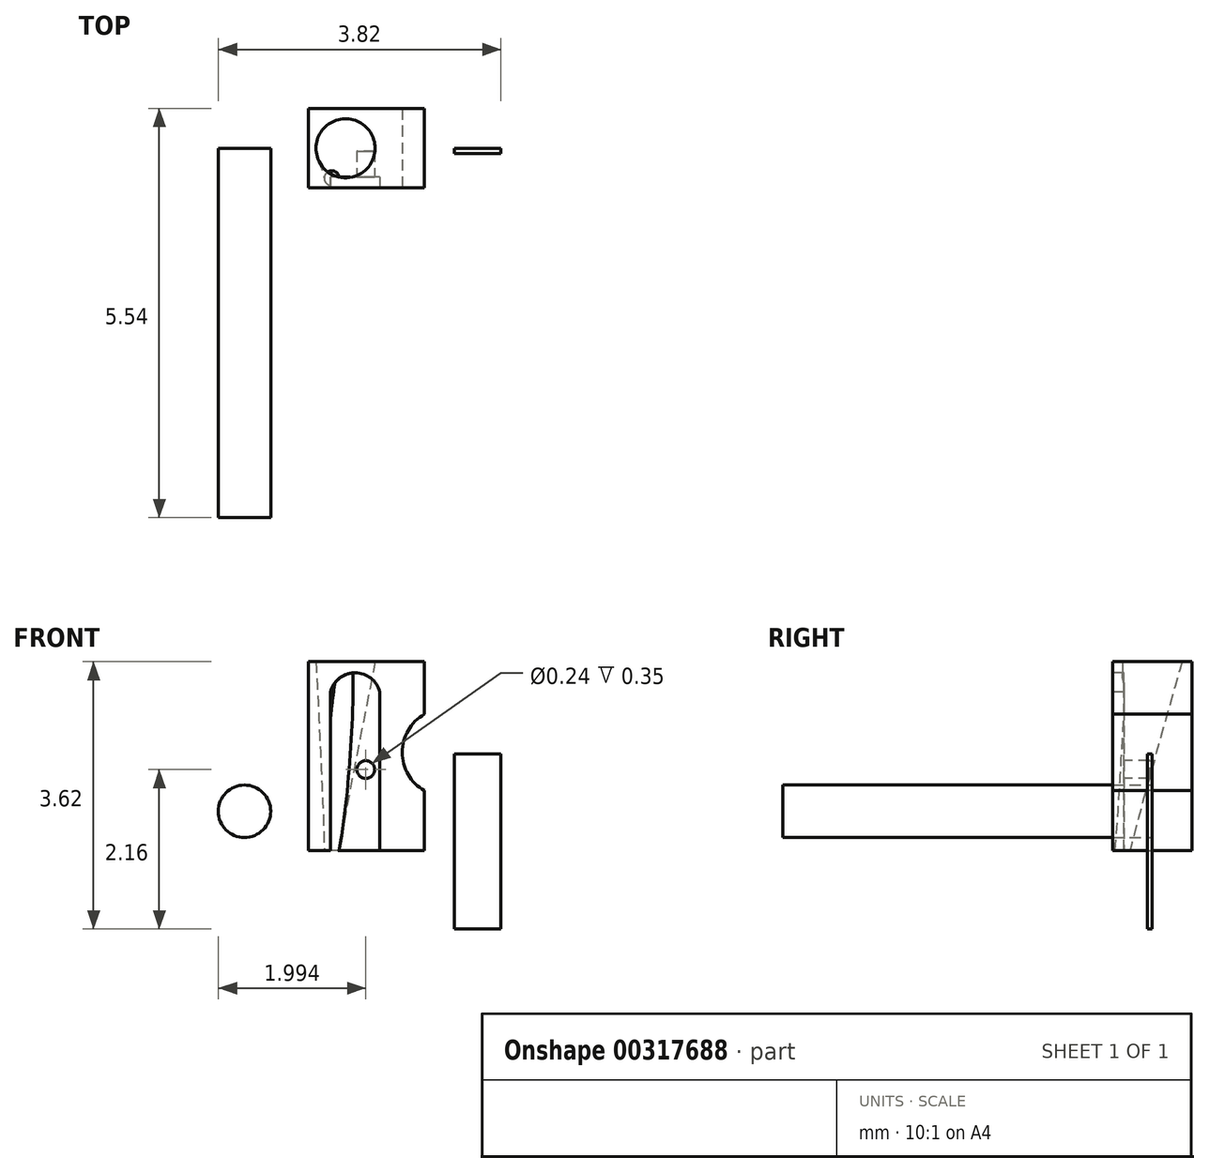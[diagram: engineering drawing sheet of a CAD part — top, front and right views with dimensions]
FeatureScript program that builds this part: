
annotation { "Feature Type Name" : "Feature", "Feature Type Description" : "" }
export const myFeature = defineFeature(function(context is Context, id is Id, definition is map)
    precondition{}
    {
        {
            var Q0;
            Q0=qCreatedBy(makeId("Top.planeOp"),FACE);
            var sketch = newSketch(context, id + "F0", { "sketchPlane" : qUnion([Q0])});
            skLineSegment(sketch, "E0.bottom", {"start": v(0.5, -0.54) * mm, "end": v(-0.5, -0.54) * mm});
            skLineSegment(sketch, "E0.top", {"start": v(0.5, 0.54) * mm, "end": v(-0.5, 0.54) * mm});
            skLineSegment(sketch, "E0.left", {"start": v(0.5, -0.54) * mm, "end": v(0.5, 0.54) * mm});
            skLineSegment(sketch, "E0.right", {"start": v(-0.5, -0.54) * mm, "end": v(-0.5, 0.54) * mm});
            skPoint(sketch, "E0.middle", {"position": v(0, 0) * mm});
            skLineSegment(sketch, "E1", {"start": v(0.5, 0.54) * mm, "end": v(1.07, 0.54) * mm});
            skLineSegment(sketch, "E2", {"start": v(0.5, -0.54) * mm, "end": v(1.07, -0.54) * mm});
            skLineSegment(sketch, "E3", {"start": v(1.07, -0.54) * mm, "end": v(1.07, 0.54) * mm});
            skLineSegment(sketch, "E4", {"start": v(1.07, 0) * mm, "end": v(-0.5, 0) * mm});
            skSolve(sketch);
        }
        {
            var Q0;
            Q0 = qSketchRegion(id + "F0", true);
            extrude(context, id + "F1", {"entities" : qUnion([Q0]), "depth" : 2.56 * mm});
        }
        {
            var Q0;
            Q0=makeQuery(id+"F1.opExtrude","SWEPT_FACE",FACE,{"disambiguationData":[OSD([sQuery(id+"F0.wireOp",EDGE,"E0.bottom"),sQuery(id+"F0.wireOp",EDGE,"E2")])]});
            var sketch = newSketch(context, id + "F2", { "sketchPlane" : qUnion([Q0])});
            skLineSegment(sketch, "E5", {"start": v(-0.5, 0.1) * mm, "end": v(-0.2, 0.1) * mm});
            skLineSegment(sketch, "E6", {"start": v(1.07, 0.1) * mm, "end": v(0.47, 0.1) * mm});
            skLineSegment(sketch, "E7", {"start": v(0.47, 2.56) * mm, "end": v(0.47, 2.41) * mm});
            skLineSegment(sketch, "E8", {"start": v(0.47, 2.41) * mm, "end": v(-0.2, 2.41) * mm});
            skLineSegment(sketch, "E9", {"start": v(-0.2, 2.41) * mm, "end": v(-0.2, 2.56) * mm});
            skLineSegment(sketch, "E10", {"start": v(0.13, 2.41) * mm, "end": v(0.13, 2.15) * mm});
            skArc(sketch, "E11", {"start": v(0.47, 2.15) * mm, "mid": v(0.13, 2.41) * mm, "end": v(-0.2, 2.15) * mm});
            skLineSegment(sketch, "E12", {"start": v(0.47, 2.15) * mm, "end": v(0.47, 0.1) * mm});
            skLineSegment(sketch, "E13", {"start": v(-0.2, 2.15) * mm, "end": v(-0.2, 0.1) * mm});
            skLineSegment(sketch, "E14", {"start": v(0.47, 0.1) * mm, "end": v(0.47, 0) * mm});
            skLineSegment(sketch, "E15", {"start": v(-0.2, 0.1) * mm, "end": v(-0.2, 0) * mm});
            skSolve(sketch);
        }
        {
            var Q0;
            {var subQ1=sQuery(id+"F2.wireOp",EDGE,"E12");Q0=makeQuery(id+"F2.imprint","IMPRINT",FACE,{"disambiguationData":[TD([[makeQuery(id+"F2.imprint","IMPRINT",EDGE,{"derivedFrom":subQ1}),-1.0]])]});}
            extrude(context, id + "F3", {"entities" : qUnion([Q0]), "operationType" : NewBodyOperationType.REMOVE, "oppositeDirection" : true, "depth" : 0.15 * mm});
        }
        {
            var Q0;
            Q0=makeQuery(id+"F1.opExtrude","CAP_FACE",FACE,{"disambiguationData":[OSD([sQuery(id+"F0.wireOp",EDGE,"E0.bottom"),sQuery(id+"F0.wireOp",EDGE,"E0.top"),sQuery(id+"F0.wireOp",EDGE,"E0.right"),sQuery(id+"F0.wireOp",EDGE,"E1"),sQuery(id+"F0.wireOp",EDGE,"E2"),sQuery(id+"F0.wireOp",EDGE,"E3")])],"isStart":false});
            var sketch = newSketch(context, id + "F4", { "sketchPlane" : qUnion([Q0])});
            skCircle(sketch, "E16", {"center": v(0, 0) * mm, "radius": 0.4 * mm});
            skSolve(sketch);
        }
        {
            var Q0;
            {var subQ0=sQuery(id+"F0.wireOp",EDGE,"E1");Q0=makeQuery(id+"F0.imprint","IMPRINT",FACE,{"disambiguationData":[TD([[makeQuery(id+"F0.imprint","IMPRINT",EDGE,{"derivedFrom":subQ0}),-1.0]])]});}
            var sketch = newSketch(context, id + "F5", { "sketchPlane" : qUnion([Q0])});
            skCircle(sketch, "E17", {"center": v(-0.19, -0.4) * mm, "radius": 0.1 * mm});
            skSolve(sketch);
        }
        {
            var Q0;
            Q0 = qSketchRegion(id + "F5", true);
            extrude(context, id + "F6", {"entities" : qUnion([Q0]), "operationType" : NewBodyOperationType.REMOVE, "oppositeDirection" : true, "depth" : 0.7 * mm});
        }
        {
            var Q1;
            Q1=makeQuery(id+"F4.imprint","IMPRINT",FACE,{"disambiguationData":[TD([[makeQuery(id+"F4.imprint","IMPRINT",EDGE,{"derivedFrom":sQuery(id+"F4.wireOp",EDGE,"E16")}),1.0]])]});
            var Q2;
            Q2 = qSketchRegion(id + "F5", true);
            loft(context, id + "F7", {"operationType" : NewBodyOperationType.REMOVE, "sheetProfilesArray" : [{ "sheetProfileEntities" : qUnion([Q1]) }, { "sheetProfileEntities" : qUnion([Q2]) }]});
        }
        {
            var Q0;
            Q0=qCreatedBy(makeId("Front.planeOp"),FACE);
            var sketch = newSketch(context, id + "F8", { "sketchPlane" : qUnion([Q0])});
            skArc(sketch, "E18", {"start": v(1.08, 1.86) * mm, "mid": v(0.77, 1.33) * mm, "end": v(1.08, 0.8) * mm});
            skLineSegment(sketch, "E19", {"start": v(1.08, 1.86) * mm, "end": v(1.08, 0.8) * mm});
            skSolve(sketch);
        }
        {
            var Q0;
            Q0 = qSketchRegion(id + "F8", true);
            extrude(context, id + "F9", {"entities" : qUnion([Q0]), "operationType" : NewBodyOperationType.REMOVE, "endBound" : BoundingType.SYMMETRIC, "oppositeDirection" : true, "depth" : 20 * mm});
        }
        {
            var Q0;
            {var subQ1=sQuery(id+"F2.wireOp",EDGE,"E12");Q0=makeQuery(id+"F2.imprint","IMPRINT",FACE,{"disambiguationData":[TD([[makeQuery(id+"F2.imprint","IMPRINT",EDGE,{"derivedFrom":subQ1}),-1.0]])]});}
            var sketch = newSketch(context, id + "F10", { "sketchPlane" : qUnion([Q0])});
            skCircle(sketch, "E20", {"center": v(0.27, 1.1) * mm, "radius": 0.12 * mm});
            skPoint(sketch, "E21.start.orphan", {"position": v(0.15, 0) * mm});
            skPoint(sketch, "E22.start.orphan", {"position": v(0.05, 1.1) * mm});
            skPoint(sketch, "E23.start.orphan", {"position": v(0.15, 1.1) * mm});
            skSolve(sketch);
        }
        {
            var Q0;
            Q0 = qSketchRegion(id + "F10", true);
            extrude(context, id + "F11", {"entities" : qUnion([Q0]), "operationType" : NewBodyOperationType.REMOVE, "oppositeDirection" : true, "depth" : 0.5 * mm});
        }
        {
            var Q0;
            Q0=qCreatedBy(makeId("Front.planeOp"),FACE);
            var sketch = newSketch(context, id + "F12", { "sketchPlane" : qUnion([Q0])});
            skCircle(sketch, "E24", {"center": v(-1.37, 0.53) * mm, "radius": 0.35 * mm});
            skSolve(sketch);
        }
        {
            var Q0;
            Q0=makeQuery(id+"F12.imprint","IMPRINT",FACE,{"disambiguationData":[TD([[makeQuery(id+"F12.imprint","IMPRINT",EDGE,{"derivedFrom":sQuery(id+"F12.wireOp",EDGE,"E24")}),1.0]])]});
            extrude(context, id + "F13", {"entities" : qUnion([Q0]), "depth" : 5 * mm});
        }
        {
            var Q0;
            Q0=qCreatedBy(makeId("Front.planeOp"),FACE);
            var sketch = newSketch(context, id + "F14", { "sketchPlane" : qUnion([Q0])});
            skLineSegment(sketch, "E25.bottom", {"start": v(1.47, 1.31) * mm, "end": v(2.1, 1.31) * mm});
            skLineSegment(sketch, "E25.top", {"start": v(1.47, -1.06) * mm, "end": v(2.1, -1.06) * mm});
            skLineSegment(sketch, "E25.left", {"start": v(1.47, 1.31) * mm, "end": v(1.47, -1.06) * mm});
            skLineSegment(sketch, "E25.right", {"start": v(2.1, 1.31) * mm, "end": v(2.1, -1.06) * mm});
            skSolve(sketch);
        }
        {
            var Q0;
            Q0 = qSketchRegion(id + "F14", true);
            extrude(context, id + "F15", {"entities" : qUnion([Q0]), "depth" : 0.07 * mm});
        }
    });
